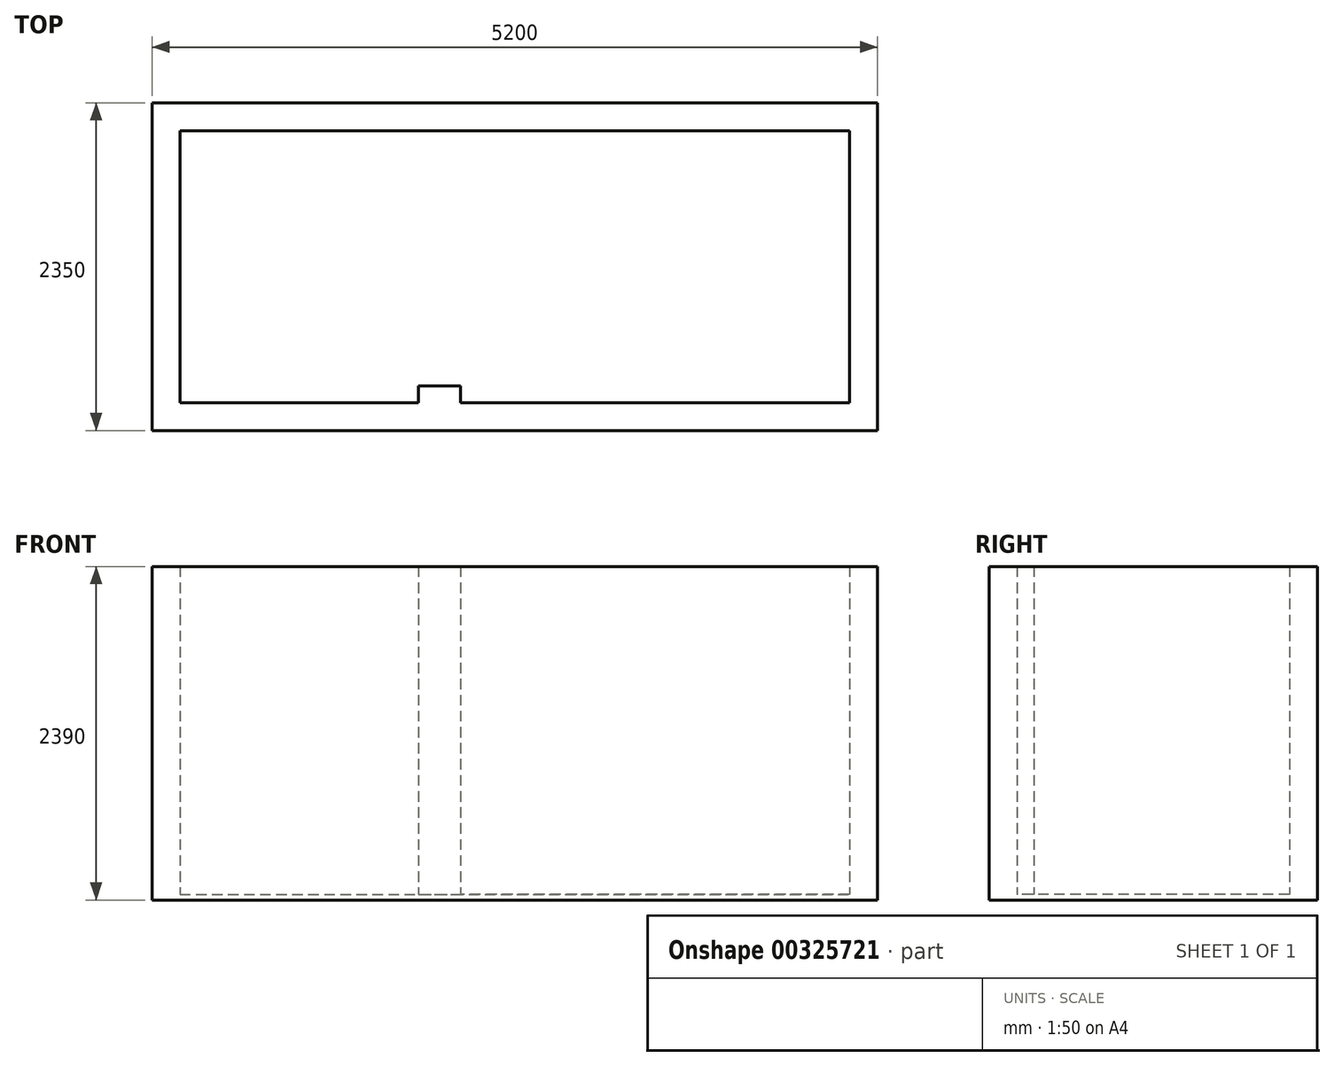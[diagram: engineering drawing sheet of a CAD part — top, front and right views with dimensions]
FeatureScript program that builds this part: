
annotation { "Feature Type Name" : "Feature", "Feature Type Description" : "" }
export const myFeature = defineFeature(function(context is Context, id is Id, definition is map)
    precondition{}
    {
        {
            var Q0;
            Q0=qCreatedBy(makeId("Top.planeOp"),FACE);
            var sketch = newSketch(context, id + "F0", { "sketchPlane" : qUnion([Q0])});
            skLineSegment(sketch, "E0", {"start": v(-2396.73, 46.06) * mm, "end": v(2403.27, 46.06) * mm});
            skLineSegment(sketch, "E1", {"start": v(-2396.73, 46.06) * mm, "end": v(-2396.73, -1903.94) * mm});
            skLineSegment(sketch, "E2", {"start": v(-2396.73, -1903.94) * mm, "end": v(-1496.73, -1903.94) * mm});
            skLineSegment(sketch, "E3", {"start": v(-1496.73, -1903.94) * mm, "end": v(-736.73, -1903.94) * mm});
            skLineSegment(sketch, "E4", {"start": v(-736.73, -1903.94) * mm, "end": v(-686.73, -1903.94) * mm});
            skLineSegment(sketch, "E5", {"start": v(-686.73, -1903.94) * mm, "end": v(-686.73, -1783.94) * mm});
            skLineSegment(sketch, "E6", {"start": v(-686.73, -1783.94) * mm, "end": v(-386.73, -1783.94) * mm});
            skLineSegment(sketch, "E7", {"start": v(-386.73, -1783.94) * mm, "end": v(-386.73, -1903.94) * mm});
            skLineSegment(sketch, "E8", {"start": v(2403.27, 46.06) * mm, "end": v(2403.27, -1903.94) * mm});
            skLineSegment(sketch, "E9", {"start": v(2403.27, -1903.94) * mm, "end": v(-386.73, -1903.94) * mm});
            skPoint(sketch, "E10.start.orphan", {"position": v(-706.73, -1883.94) * mm});
            skPoint(sketch, "E11.start.orphan", {"position": v(-366.73, -1883.94) * mm});
            skLineSegment(sketch, "E12", {"start": v(-2596.73, 246.06) * mm, "end": v(2603.27, 246.06) * mm});
            skLineSegment(sketch, "E13", {"start": v(2603.27, 246.06) * mm, "end": v(2603.27, -2103.94) * mm});
            skLineSegment(sketch, "E14", {"start": v(2603.27, -2103.94) * mm, "end": v(-2596.73, -2103.94) * mm});
            skLineSegment(sketch, "E15", {"start": v(-2596.73, -2103.94) * mm, "end": v(-2596.73, 246.06) * mm});
            skSolve(sketch);
        }
        {
            var Q0;
            Q0=makeQuery(id+"F0.imprint","IMPRINT",FACE,{"disambiguationData":[TD([[makeQuery(id+"F0.imprint","IMPRINT",EDGE,{"derivedFrom":sQuery(id+"F0.wireOp",EDGE,"E0")}),1.0]])]});
            extrude(context, id + "F1", {"entities" : qUnion([Q0]), "depth" : 2350 * mm});
        }
        {
            var Q0;
            Q0=makeQuery(id+"F1.opExtrude","CAP_FACE",FACE,{"disambiguationData":[OSD([sQuery(id+"F0.wireOp",EDGE,"E0"),sQuery(id+"F0.wireOp",EDGE,"E1"),sQuery(id+"F0.wireOp",EDGE,"E2"),sQuery(id+"F0.wireOp",EDGE,"E3"),sQuery(id+"F0.wireOp",EDGE,"E4"),sQuery(id+"F0.wireOp",EDGE,"E5"),sQuery(id+"F0.wireOp",EDGE,"E6"),sQuery(id+"F0.wireOp",EDGE,"E7"),sQuery(id+"F0.wireOp",EDGE,"E8"),sQuery(id+"F0.wireOp",EDGE,"E9"),sQuery(id+"F0.wireOp",EDGE,"E12"),sQuery(id+"F0.wireOp",EDGE,"E13"),sQuery(id+"F0.wireOp",EDGE,"E14"),sQuery(id+"F0.wireOp",EDGE,"E15")])],"isStart":true});
            var sketch = newSketch(context, id + "F2", { "sketchPlane" : qUnion([Q0])});
            skLineSegment(sketch, "E16", {"start": v(-2596.73, 2103.94) * mm, "end": v(-2596.73, -246.06) * mm});
            skLineSegment(sketch, "E17", {"start": v(-2596.73, -246.06) * mm, "end": v(2603.27, -246.06) * mm});
            skLineSegment(sketch, "E18", {"start": v(2603.27, -246.06) * mm, "end": v(2603.27, 2103.94) * mm});
            skLineSegment(sketch, "E19", {"start": v(2603.27, 2103.94) * mm, "end": v(-2596.73, 2103.94) * mm});
            skSolve(sketch);
        }
        {
            var Q0;
            Q0 = qSketchRegion(id + "F2", true);
            extrude(context, id + "F3", {"entities" : qUnion([Q0]), "operationType" : NewBodyOperationType.ADD, "depth" : 40 * mm});
        }
    });
